# Revit family: RFA_Line
name_source: partatom
category: Armazón estructural
units: mm (PartAtom-declared; Revit-internal decimal feet)

## family parameters
Compartido = No
Corte con vacíos al cargar = No
Exportar siempre como geometría = No
Forma de sección = Sin definir
Material para comportamiento de modelo = Otro
Mostrar corte previo de familia en vistas de plano = Sí
Redondeo de longitud de armazón estructural = 0 mm
Representación simbólica = Desde familia
Se basa en plano de trabajo = No
Siempre vertical = Sí

## types (6) — shared parameters
zero-valued in all types: Elevación por defecto

## per-type parameters (varying)
| type | M·Width |
| M·WallBeamDiagonal·1050mm | 1050 mm |
| M·WallBeamDiagonal·1575mm | 1575 mm  [stored 5.16732 ft] |
| M·WallBeamDiagonal·2100mm | 2100 mm |
| M·WallBeamDiagonal·2625mm | 2625 mm |
| M·WallBeamDiagonal·3150mm | 3150 mm |
| M·WallBeamDiagonal·3675mm | 3675 mm |

note: [stored X ft] marks values corroborated as IEEE doubles in the binary element streams (Revit-internal decimal feet)

## geometry (parser evidence)
native form markers: Blend x8
no freeform markers — native parametric forms only
